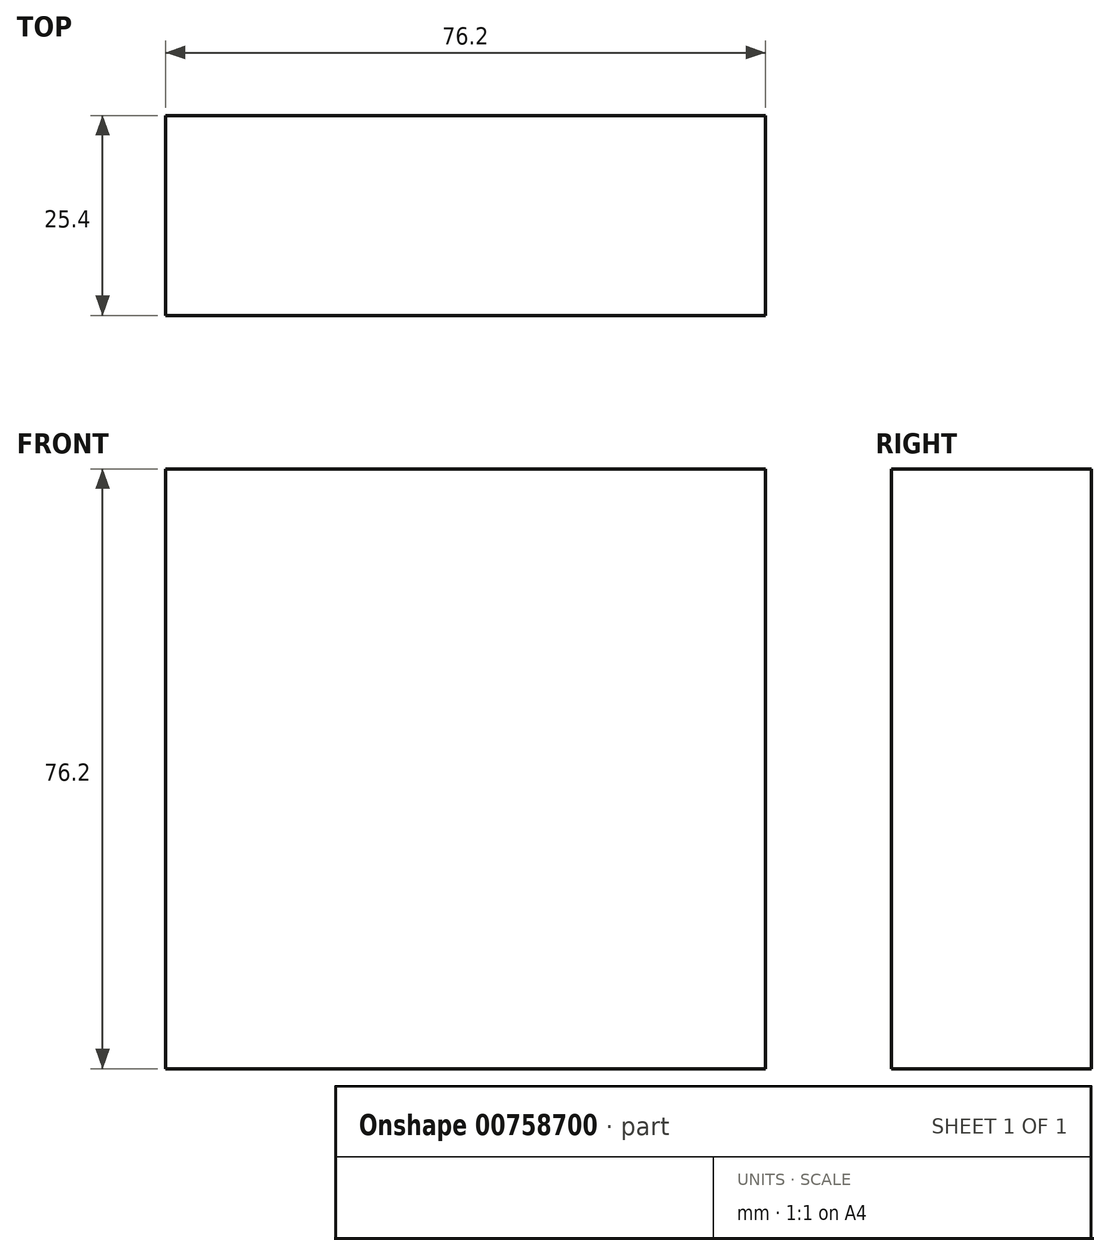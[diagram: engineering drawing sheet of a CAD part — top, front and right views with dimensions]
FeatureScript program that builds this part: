
annotation { "Feature Type Name" : "Feature", "Feature Type Description" : "" }
export const myFeature = defineFeature(function(context is Context, id is Id, definition is map)
    precondition{}
    {
        {
            var Q0;
            Q0=qCreatedBy(makeId("Front.planeOp"),FACE);
            var sketch = newSketch(context, id + "F0", { "sketchPlane" : qUnion([Q0])});
            skLineSegment(sketch, "E0.bottom", {"start": v(-8.54, 50.66) * mm, "end": v(67.66, 50.66) * mm});
            skLineSegment(sketch, "E0.top", {"start": v(-8.54, -25.54) * mm, "end": v(67.66, -25.54) * mm});
            skLineSegment(sketch, "E0.left", {"start": v(-8.54, 50.66) * mm, "end": v(-8.54, -25.54) * mm});
            skLineSegment(sketch, "E0.right", {"start": v(67.66, 50.66) * mm, "end": v(67.66, -25.54) * mm});
            skSolve(sketch);
        }
        {
            var Q0;
            Q0=makeQuery(id+"F0.imprint","IMPRINT",FACE,{"disambiguationData":[TD([[makeQuery(id+"F0.imprint","IMPRINT",EDGE,{"derivedFrom":sQuery(id+"F0.wireOp",EDGE,"E0.bottom")}),-1.0]])]});
            extrude(context, id + "F1", {"entities" : qUnion([Q0]), "depth" : 25.4 * mm, "offsetDistance" : 25.4 * mm});
        }
    });
